# Revit family: Турникет трипод PERCo_T-5
name_source: partatom
category: Mechanical Equipment
units: mm (PartAtom-declared; Revit-internal decimal feet)

## family parameters
Always vertical = No
Classification = None
Cut with Voids When Loaded = No
Part Type = Normal
Room Calculation Point = No
Round Connector Dimension = Use Diameter
Shared = No
Work Plane-Based = No

## types (1)
- T-5
    Built-in reader = not provided
    Colour = RAL 7032
    Current = 1 A
    Dimensions = 870×836×1026
    Electrical connection = 220 V
    Full name = T-5 Electromechanical Tripod Turnstile
    Housing material = White
    IP Code = IP41
    Manufacturer = PERCo
    Material = Housing ─ powder-coated steel. Barrier arms ─ painted steel (black colour) or stainless steel.
    Maximum dimensions of ACS controller = not provided
    Maximum dimensions of installed readers = not provided
    Name = T-5 Tripod Turnstile
    Number = 1
    Operating temperature = from +1°С to +50°С
    Operating voltage = 12 V
    Passageway width = 500 mm for AS-05 Barrier arms, 600 mm - for other types of barrier arms
    Plank material_04 = Stainless steel
    Plank material_05 = Black
    Rated power = 9 W
    Throughput rate = 30 persons/min
    Type1 = - : PERCo-AS-05
    URL = https://www.perco.com
    Unit of measurement = pcs
    Weight = max. 22 kg
